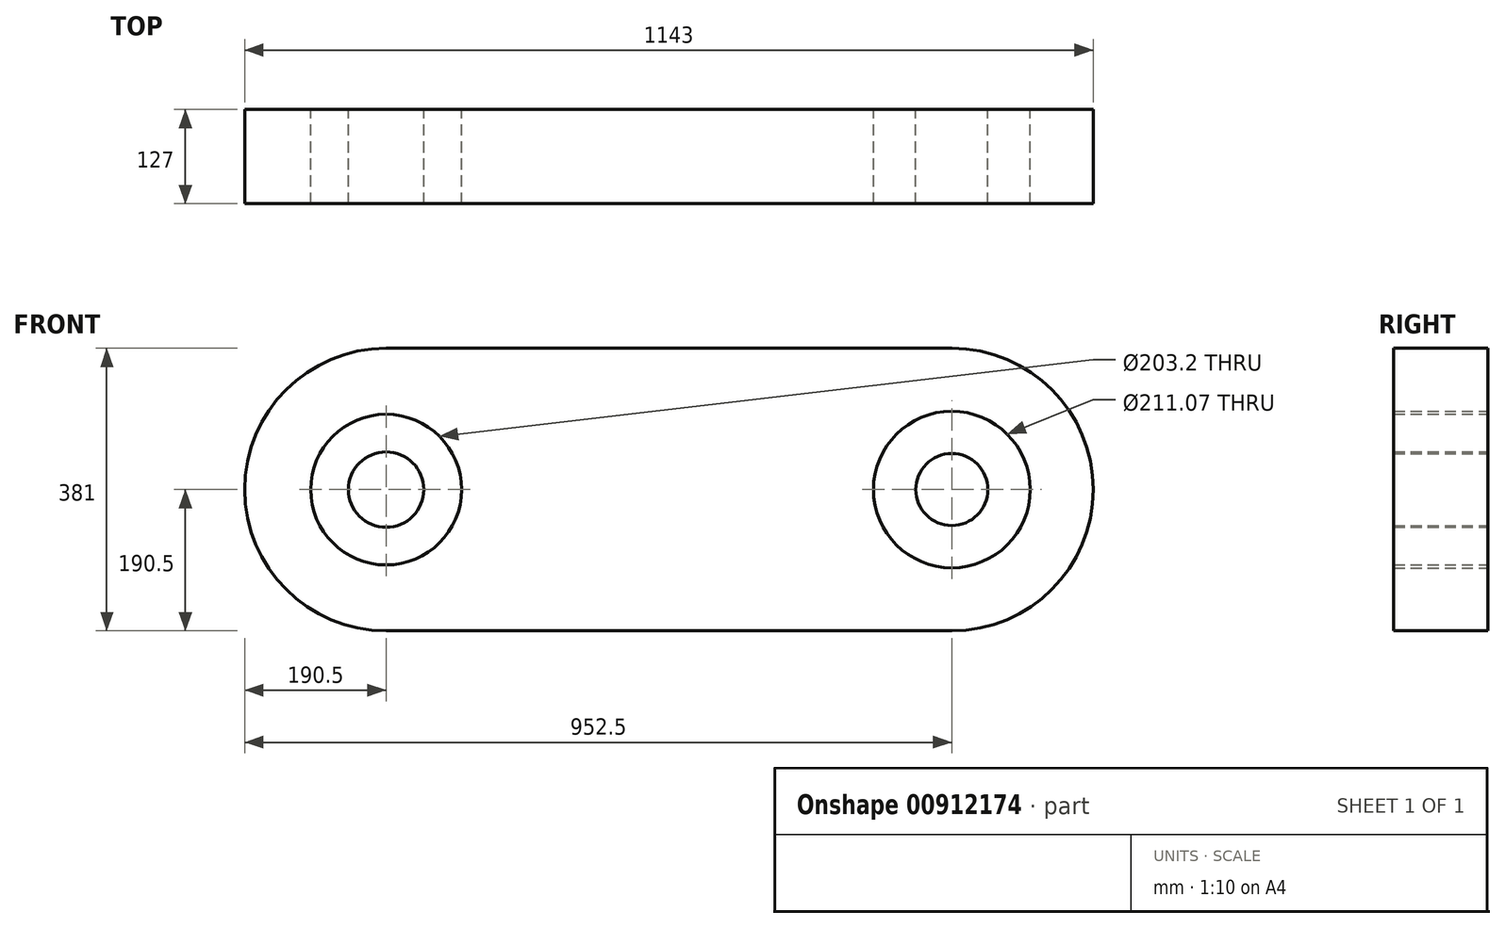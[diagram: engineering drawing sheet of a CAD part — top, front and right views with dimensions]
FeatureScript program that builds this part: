
annotation { "Feature Type Name" : "Feature", "Feature Type Description" : "" }
export const myFeature = defineFeature(function(context is Context, id is Id, definition is map)
    precondition{}
    {
        {
            var Q0;
            Q0=qCreatedBy(makeId("Front.planeOp"),FACE);
            var sketch = newSketch(context, id + "F0", { "sketchPlane" : qUnion([Q0])});
            skLineSegment(sketch, "E0.bottom", {"start": v(0, 0) * mm, "end": v(762, 0) * mm});
            skLineSegment(sketch, "E0.top", {"start": v(0, 381) * mm, "end": v(762, 381) * mm});
            skArc(sketch, "E1", {"start": v(0, 381) * mm, "mid": v(-190.5, 190.5) * mm, "end": v(0, 0) * mm});
            skArc(sketch, "E2", {"start": v(762, 0) * mm, "mid": v(952.5, 190.5) * mm, "end": v(762, 381) * mm});
            skCircle(sketch, "E3", {"center": v(0, 190.5) * mm, "radius": 101.6 * mm});
            skCircle(sketch, "E4", {"center": v(0, 190.5) * mm, "radius": 50.8 * mm});
            skCircle(sketch, "E5", {"center": v(762, 190.5) * mm, "radius": 105.54 * mm});
            skCircle(sketch, "E6", {"center": v(762, 190.5) * mm, "radius": 48.51 * mm});
            skSolve(sketch);
        }
        {
            var Q0;
            Q0 = qSketchRegion(id + "F0", true);
            var Q1;
            Q1=makeQuery(id+"F0.imprint","IMPRINT",FACE,{"disambiguationData":[TD([[makeQuery(id+"F0.imprint","IMPRINT",EDGE,{"derivedFrom":sQuery(id+"F0.wireOp",EDGE,"E4")}),1.0]])]});
            var Q2;
            Q2=makeQuery(id+"F0.imprint","IMPRINT",FACE,{"disambiguationData":[TD([[makeQuery(id+"F0.imprint","IMPRINT",EDGE,{"derivedFrom":sQuery(id+"F0.wireOp",EDGE,"E6")}),1.0]])]});
            extrude(context, id + "F1", {"entities" : qUnion([Q0, Q1, Q2]), "depth" : 127 * mm, "offsetDistance" : 25.4 * mm});
        }
    });
